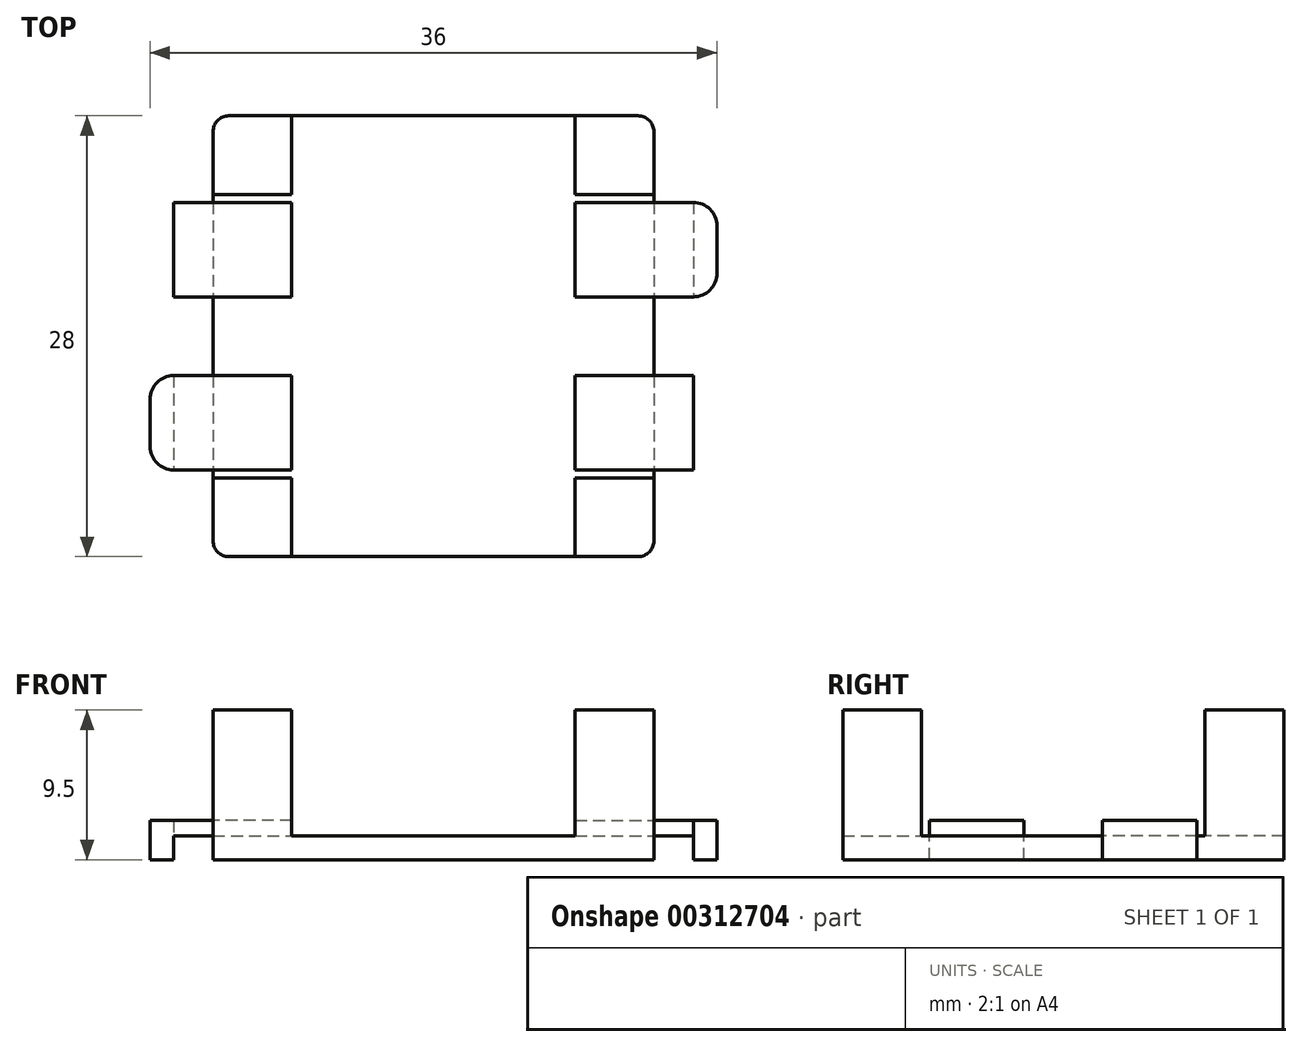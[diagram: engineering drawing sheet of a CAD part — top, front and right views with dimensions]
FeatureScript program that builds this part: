
annotation { "Feature Type Name" : "Feature", "Feature Type Description" : "" }
export const myFeature = defineFeature(function(context is Context, id is Id, definition is map)
    precondition{}
    {
        {
            var Q0;
            Q0=qCreatedBy(makeId("Top.planeOp"),FACE);
            var sketch = newSketch(context, id + "F0", { "sketchPlane" : qUnion([Q0])});
            skLineSegment(sketch, "E0.bottom", {"start": v(0, 0) * mm, "end": v(28, 0) * mm});
            skLineSegment(sketch, "E0.top", {"start": v(0, -28) * mm, "end": v(28, -28) * mm});
            skLineSegment(sketch, "E0.left", {"start": v(0, 0) * mm, "end": v(0, -28) * mm});
            skLineSegment(sketch, "E0.right", {"start": v(28, 0) * mm, "end": v(28, -28) * mm});
            skSolve(sketch);
        }
        {
            var Q0;
            Q0=makeQuery(id+"F0.imprint","IMPRINT",FACE,{"disambiguationData":[TD([[makeQuery(id+"F0.imprint","IMPRINT",EDGE,{"derivedFrom":sQuery(id+"F0.wireOp",EDGE,"E0.bottom")}),-1.0]])]});
            extrude(context, id + "F1", {"entities" : qUnion([Q0]), "depth" : 1.5 * mm});
        }
        {
            var Q0;
            Q0=makeQuery(id+"F1.opExtrude","CAP_FACE",FACE,{"disambiguationData":[OSD([sQuery(id+"F0.wireOp",EDGE,"E0.bottom"),sQuery(id+"F0.wireOp",EDGE,"E0.top"),sQuery(id+"F0.wireOp",EDGE,"E0.left"),sQuery(id+"F0.wireOp",EDGE,"E0.right")])],"isStart":false});
            var sketch = newSketch(context, id + "F2", { "sketchPlane" : qUnion([Q0])});
            skLineSegment(sketch, "E1.bottom", {"start": v(0, -28) * mm, "end": v(5, -28) * mm});
            skLineSegment(sketch, "E1.top", {"start": v(0, -23) * mm, "end": v(5, -23) * mm});
            skLineSegment(sketch, "E1.left", {"start": v(0, -28) * mm, "end": v(0, -23) * mm});
            skLineSegment(sketch, "E1.right", {"start": v(5, -28) * mm, "end": v(5, -23) * mm});
            skLineSegment(sketch, "E2.bottom", {"start": v(0, 0) * mm, "end": v(5, 0) * mm});
            skLineSegment(sketch, "E2.top", {"start": v(0, -5) * mm, "end": v(5, -5) * mm});
            skLineSegment(sketch, "E2.left", {"start": v(0, 0) * mm, "end": v(0, -5) * mm});
            skLineSegment(sketch, "E2.right", {"start": v(5, 0) * mm, "end": v(5, -5) * mm});
            skLineSegment(sketch, "E3.bottom", {"start": v(28, 0) * mm, "end": v(23, 0) * mm});
            skLineSegment(sketch, "E3.top", {"start": v(28, -5) * mm, "end": v(23, -5) * mm});
            skLineSegment(sketch, "E3.left", {"start": v(28, 0) * mm, "end": v(28, -5) * mm});
            skLineSegment(sketch, "E3.right", {"start": v(23, 0) * mm, "end": v(23, -5) * mm});
            skLineSegment(sketch, "E4.bottom", {"start": v(28, -28) * mm, "end": v(23, -28) * mm});
            skLineSegment(sketch, "E4.top", {"start": v(28, -23) * mm, "end": v(23, -23) * mm});
            skLineSegment(sketch, "E4.left", {"start": v(28, -28) * mm, "end": v(28, -23) * mm});
            skLineSegment(sketch, "E4.right", {"start": v(23, -28) * mm, "end": v(23, -23) * mm});
            skSolve(sketch);
        }
        {
            var Q0;
            Q0=makeQuery(id+"F2.imprint","IMPRINT",FACE,{"disambiguationData":[TD([[makeQuery(id+"F2.imprint","IMPRINT",EDGE,{"derivedFrom":sQuery(id+"F2.wireOp",EDGE,"E2.bottom")}),-1.0]])]});
            var Q1;
            Q1=makeQuery(id+"F2.imprint","IMPRINT",FACE,{"disambiguationData":[TD([[makeQuery(id+"F2.imprint","IMPRINT",EDGE,{"derivedFrom":sQuery(id+"F2.wireOp",EDGE,"E3.bottom")}),-1.0]])]});
            var Q2;
            Q2=makeQuery(id+"F2.imprint","IMPRINT",FACE,{"disambiguationData":[TD([[makeQuery(id+"F2.imprint","IMPRINT",EDGE,{"derivedFrom":sQuery(id+"F2.wireOp",EDGE,"E4.bottom")}),1.0]])]});
            var Q3;
            Q3=makeQuery(id+"F2.imprint","IMPRINT",FACE,{"disambiguationData":[TD([[makeQuery(id+"F2.imprint","IMPRINT",EDGE,{"derivedFrom":sQuery(id+"F2.wireOp",EDGE,"E1.bottom")}),1.0]])]});
            extrude(context, id + "F3", {"entities" : qUnion([Q0, Q1, Q2, Q3]), "operationType" : NewBodyOperationType.ADD, "depth" : 8 * mm});
        }
        {
            var Q0;
            Q0=makeQuery(id+"F3.boolean.opBoolean","MERGE",EDGE,{"derivedFrom":[makeQuery(id+"F1.opExtrude","SWEPT_EDGE",EDGE,{"disambiguationData":[OSD([sQuery(id+"F0.wireOp",EDGE,"E0.top"),sQuery(id+"F0.wireOp",EDGE,"E0.left")])]}),makeQuery(id+"F3.opExtrude","SWEPT_EDGE",EDGE,{"disambiguationData":[OSD([sQuery(id+"F2.wireOp",EDGE,"E1.bottom"),sQuery(id+"F2.wireOp",EDGE,"E1.left")])]})]});
            var Q1;
            Q1=makeQuery(id+"F3.boolean.opBoolean","MERGE",EDGE,{"derivedFrom":[makeQuery(id+"F1.opExtrude","SWEPT_EDGE",EDGE,{"disambiguationData":[OSD([sQuery(id+"F0.wireOp",EDGE,"E0.bottom"),sQuery(id+"F0.wireOp",EDGE,"E0.left")])]}),makeQuery(id+"F3.opExtrude","SWEPT_EDGE",EDGE,{"disambiguationData":[OSD([sQuery(id+"F2.wireOp",EDGE,"E2.bottom"),sQuery(id+"F2.wireOp",EDGE,"E2.left")])]})]});
            var Q2;
            Q2=makeQuery(id+"F3.boolean.opBoolean","MERGE",EDGE,{"derivedFrom":[makeQuery(id+"F1.opExtrude","SWEPT_EDGE",EDGE,{"disambiguationData":[OSD([sQuery(id+"F0.wireOp",EDGE,"E0.bottom"),sQuery(id+"F0.wireOp",EDGE,"E0.right")])]}),makeQuery(id+"F3.opExtrude","SWEPT_EDGE",EDGE,{"disambiguationData":[OSD([sQuery(id+"F2.wireOp",EDGE,"E3.bottom"),sQuery(id+"F2.wireOp",EDGE,"E3.left")])]})]});
            var Q3;
            Q3=makeQuery(id+"F3.boolean.opBoolean","MERGE",EDGE,{"derivedFrom":[makeQuery(id+"F1.opExtrude","SWEPT_EDGE",EDGE,{"disambiguationData":[OSD([sQuery(id+"F0.wireOp",EDGE,"E0.top"),sQuery(id+"F0.wireOp",EDGE,"E0.right")])]}),makeQuery(id+"F3.opExtrude","SWEPT_EDGE",EDGE,{"disambiguationData":[OSD([sQuery(id+"F2.wireOp",EDGE,"E4.bottom"),sQuery(id+"F2.wireOp",EDGE,"E4.left")])]})]});
            fillet(context, id + "F4", {"entities" : qUnion([Q0, Q1, Q2, Q3]), "radius" : 1 * mm, "tangentPropagation" : true, "allowEdgeOverflow" : false});
        }
        {
            var Q0;
            Q0=makeQuery(id+"F1.opExtrude","CAP_FACE",FACE,{"disambiguationData":[OSD([sQuery(id+"F0.wireOp",EDGE,"E0.bottom"),sQuery(id+"F0.wireOp",EDGE,"E0.top"),sQuery(id+"F0.wireOp",EDGE,"E0.left"),sQuery(id+"F0.wireOp",EDGE,"E0.right")])],"isStart":false});
            var sketch = newSketch(context, id + "F5", { "sketchPlane" : qUnion([Q0])});
            skLineSegment(sketch, "E5.bottom", {"start": v(5, -22.5) * mm, "end": v(-2.5, -22.5) * mm});
            skLineSegment(sketch, "E5.top", {"start": v(5, -16.5) * mm, "end": v(-2.5, -16.5) * mm});
            skLineSegment(sketch, "E5.left", {"start": v(5, -22.5) * mm, "end": v(5, -16.5) * mm});
            skLineSegment(sketch, "E5.right", {"start": v(-4, -21) * mm, "end": v(-4, -18) * mm});
            skLineSegment(sketch, "E6", {"start": v(0, -14) * mm, "end": v(28, -14) * mm, "construction": true});
            skLineSegment(sketch, "E7", {"start": v(14, -28) * mm, "end": v(14, 0) * mm, "construction": true});
            skPoint(sketch, "E8.visualSharp", {"position": v(-4, -22.5) * mm});
            skArc(sketch, "E8.filletArc", {"start": v(-4, -21) * mm, "mid": v(-3.56, -22.06) * mm, "end": v(-2.5, -22.5) * mm});
            skPoint(sketch, "E9.visualSharp", {"position": v(-4, -16.5) * mm});
            skArc(sketch, "E9.filletArc", {"start": v(-2.5, -16.5) * mm, "mid": v(-3.56, -16.94) * mm, "end": v(-4, -18) * mm});
            skLineSegment(sketch, "E10.MirrorCS", {"start": v(5, -11.5) * mm, "end": v(-2.5, -11.5) * mm});
            skArc(sketch, "E11.MirrorCS", {"start": v(-2.5, -11.5) * mm, "mid": v(-3.56, -11.06) * mm, "end": v(-4, -10) * mm});
            skLineSegment(sketch, "E12.MirrorCS", {"start": v(-4, -7) * mm, "end": v(-4, -10) * mm});
            skArc(sketch, "E13.MirrorCS", {"start": v(-4, -7) * mm, "mid": v(-3.56, -5.94) * mm, "end": v(-2.5, -5.5) * mm});
            skLineSegment(sketch, "E14.MirrorCS", {"start": v(5, -5.5) * mm, "end": v(-2.5, -5.5) * mm});
            skLineSegment(sketch, "E15.MirrorCS", {"start": v(5, -5.5) * mm, "end": v(5, -11.5) * mm});
            skLineSegment(sketch, "E16.MirrorCS", {"start": v(23, -22.5) * mm, "end": v(23, -16.5) * mm});
            skLineSegment(sketch, "E17.MirrorCS", {"start": v(23, -16.5) * mm, "end": v(30.5, -16.5) * mm});
            skArc(sketch, "E18.MirrorCS", {"start": v(30.5, -16.5) * mm, "mid": v(31.56, -16.94) * mm, "end": v(32, -18) * mm});
            skLineSegment(sketch, "E19.MirrorCS", {"start": v(32, -21) * mm, "end": v(32, -18) * mm});
            skArc(sketch, "E20.MirrorCS", {"start": v(32, -21) * mm, "mid": v(31.56, -22.06) * mm, "end": v(30.5, -22.5) * mm});
            skLineSegment(sketch, "E21.MirrorCS", {"start": v(23, -22.5) * mm, "end": v(30.5, -22.5) * mm});
            skLineSegment(sketch, "E22.MirrorCS", {"start": v(23, -5.5) * mm, "end": v(23, -11.5) * mm});
            skLineSegment(sketch, "E23.MirrorCS", {"start": v(23, -5.5) * mm, "end": v(30.5, -5.5) * mm});
            skArc(sketch, "E24.MirrorCS", {"start": v(32, -7) * mm, "mid": v(31.56, -5.94) * mm, "end": v(30.5, -5.5) * mm});
            skLineSegment(sketch, "E25.MirrorCS", {"start": v(32, -7) * mm, "end": v(32, -10) * mm});
            skArc(sketch, "E26.MirrorCS", {"start": v(30.5, -11.5) * mm, "mid": v(31.56, -11.06) * mm, "end": v(32, -10) * mm});
            skLineSegment(sketch, "E27.MirrorCS", {"start": v(23, -11.5) * mm, "end": v(30.5, -11.5) * mm});
            skLineSegment(sketch, "E28", {"start": v(30.5, -5.5) * mm, "end": v(30.5, -11.5) * mm});
            skLineSegment(sketch, "E29", {"start": v(30.5, -16.5) * mm, "end": v(30.5, -22.5) * mm});
            skLineSegment(sketch, "E30", {"start": v(-2.5, -5.5) * mm, "end": v(-2.5, -11.5) * mm});
            skLineSegment(sketch, "E31", {"start": v(-2.5, -16.5) * mm, "end": v(-2.5, -22.5) * mm});
            skSolve(sketch);
        }
        {
            var Q0;
            {var subQ0=sQuery(id+"F5.wireOp",EDGE,"E16.MirrorCS");Q0=makeQuery(id+"F5.imprint","IMPRINT",FACE,{"disambiguationData":[TD([[makeQuery(id+"F5.imprint","IMPRINT",EDGE,{"derivedFrom":subQ0}),-1.0]])]});}
            var Q1;
            {var subQ1=sQuery(id+"F5.wireOp",EDGE,"E18.MirrorCS");Q1=makeQuery(id+"F5.imprint","IMPRINT",FACE,{"disambiguationData":[TD([[makeQuery(id+"F5.imprint","IMPRINT",EDGE,{"derivedFrom":subQ1}),-1.0]])]});}
            var Q2;
            {var subQ6=sQuery(id+"F5.wireOp",EDGE,"E24.MirrorCS");Q2=makeQuery(id+"F5.imprint","IMPRINT",FACE,{"disambiguationData":[TD([[makeQuery(id+"F5.imprint","IMPRINT",EDGE,{"derivedFrom":subQ6}),1.0]])]});}
            var Q3;
            {var subQ0=sQuery(id+"F5.wireOp",EDGE,"E22.MirrorCS");Q3=makeQuery(id+"F5.imprint","IMPRINT",FACE,{"disambiguationData":[TD([[makeQuery(id+"F5.imprint","IMPRINT",EDGE,{"derivedFrom":subQ0}),1.0]])]});}
            var Q4;
            {var subQ0=sQuery(id+"F5.wireOp",EDGE,"E5.left");Q4=makeQuery(id+"F5.imprint","IMPRINT",FACE,{"disambiguationData":[TD([[makeQuery(id+"F5.imprint","IMPRINT",EDGE,{"derivedFrom":subQ0}),1.0]])]});}
            var Q5;
            {var subQ0=sQuery(id+"F5.wireOp",EDGE,"E15.MirrorCS");Q5=makeQuery(id+"F5.imprint","IMPRINT",FACE,{"disambiguationData":[TD([[makeQuery(id+"F5.imprint","IMPRINT",EDGE,{"derivedFrom":subQ0}),-1.0]])]});}
            var Q6;
            {var subQ1=sQuery(id+"F5.wireOp",EDGE,"E11.MirrorCS");Q6=makeQuery(id+"F5.imprint","IMPRINT",FACE,{"disambiguationData":[TD([[makeQuery(id+"F5.imprint","IMPRINT",EDGE,{"derivedFrom":subQ1}),-1.0]])]});}
            var Q7;
            Q7=makeQuery(id+"F5.imprint","IMPRINT",FACE,{"disambiguationData":[TD([[makeQuery(id+"F5.imprint","IMPRINT",EDGE,{"derivedFrom":sQuery(id+"F5.wireOp",EDGE,"E5.right")}),-1.0]])]});
            var Q8;
            {var subQ0=sQuery(id+"F5.wireOp",EDGE,"E28");Q8=makeQuery(id+"F5.imprint","IMPRINT",FACE,{"disambiguationData":[TD([[makeQuery(id+"F5.imprint","IMPRINT",EDGE,{"derivedFrom":subQ0}),-1.0]])]});}
            var Q9;
            {var subQ0=sQuery(id+"F5.wireOp",EDGE,"E29");Q9=makeQuery(id+"F5.imprint","IMPRINT",FACE,{"disambiguationData":[TD([[makeQuery(id+"F5.imprint","IMPRINT",EDGE,{"derivedFrom":subQ0}),-1.0]])]});}
            var Q10;
            {var subQ0=sQuery(id+"F5.wireOp",EDGE,"E31");Q10=makeQuery(id+"F5.imprint","IMPRINT",FACE,{"disambiguationData":[TD([[makeQuery(id+"F5.imprint","IMPRINT",EDGE,{"derivedFrom":subQ0}),1.0]])]});}
            var Q11;
            {var subQ0=sQuery(id+"F5.wireOp",EDGE,"E30");Q11=makeQuery(id+"F5.imprint","IMPRINT",FACE,{"disambiguationData":[TD([[makeQuery(id+"F5.imprint","IMPRINT",EDGE,{"derivedFrom":subQ0}),1.0]])]});}
            var Q12;
            Q12=makeQuery(id+"F3.opExtrude","CAP_FACE",FACE,{"disambiguationData":[OSD([sQuery(id+"F2.wireOp",EDGE,"E1.bottom"),sQuery(id+"F2.wireOp",EDGE,"E1.top"),sQuery(id+"F2.wireOp",EDGE,"E1.left"),sQuery(id+"F2.wireOp",EDGE,"E1.right")])],"isStart":false});
            extrude(context, id + "F6", {"entities" : qUnion([Q0, Q1, Q2, Q3, Q4, Q5, Q6, Q7, Q8, Q9, Q10, Q11]), "operationType" : NewBodyOperationType.ADD, "endBoundEntityFace" : qUnion([Q12]), "depth" : 1 * mm});
        }
        {
            var Q0;
            Q0=makeQuery(id+"F5.imprint","IMPRINT",FACE,{"disambiguationData":[TD([[makeQuery(id+"F5.imprint","IMPRINT",EDGE,{"derivedFrom":sQuery(id+"F5.wireOp",EDGE,"E18.MirrorCS")}),-1.0]])]});
            var Q1;
            Q1=makeQuery(id+"F5.imprint","IMPRINT",FACE,{"disambiguationData":[TD([[makeQuery(id+"F5.imprint","IMPRINT",EDGE,{"derivedFrom":sQuery(id+"F5.wireOp",EDGE,"E24.MirrorCS")}),1.0]])]});
            var Q2;
            Q2=makeQuery(id+"F5.imprint","IMPRINT",FACE,{"disambiguationData":[TD([[makeQuery(id+"F5.imprint","IMPRINT",EDGE,{"derivedFrom":sQuery(id+"F5.wireOp",EDGE,"E11.MirrorCS")}),-1.0]])]});
            var Q3;
            Q3=makeQuery(id+"F5.imprint","IMPRINT",FACE,{"disambiguationData":[TD([[makeQuery(id+"F5.imprint","IMPRINT",EDGE,{"derivedFrom":sQuery(id+"F5.wireOp",EDGE,"E5.right")}),-1.0]])]});
            var Q4;
            Q4=makeQuery(id+"F1.opExtrude","CAP_FACE",FACE,{"disambiguationData":[OSD([sQuery(id+"F0.wireOp",EDGE,"E0.bottom"),sQuery(id+"F0.wireOp",EDGE,"E0.top"),sQuery(id+"F0.wireOp",EDGE,"E0.left"),sQuery(id+"F0.wireOp",EDGE,"E0.right")])],"isStart":true});
            extrude(context, id + "F7", {"entities" : qUnion([Q0, Q1, Q2, Q3]), "operationType" : NewBodyOperationType.ADD, "endBound" : BoundingType.UP_TO_SURFACE, "oppositeDirection" : true, "endBoundEntityFace" : qUnion([Q4]), "depth" : 25 * mm});
        }
    });
